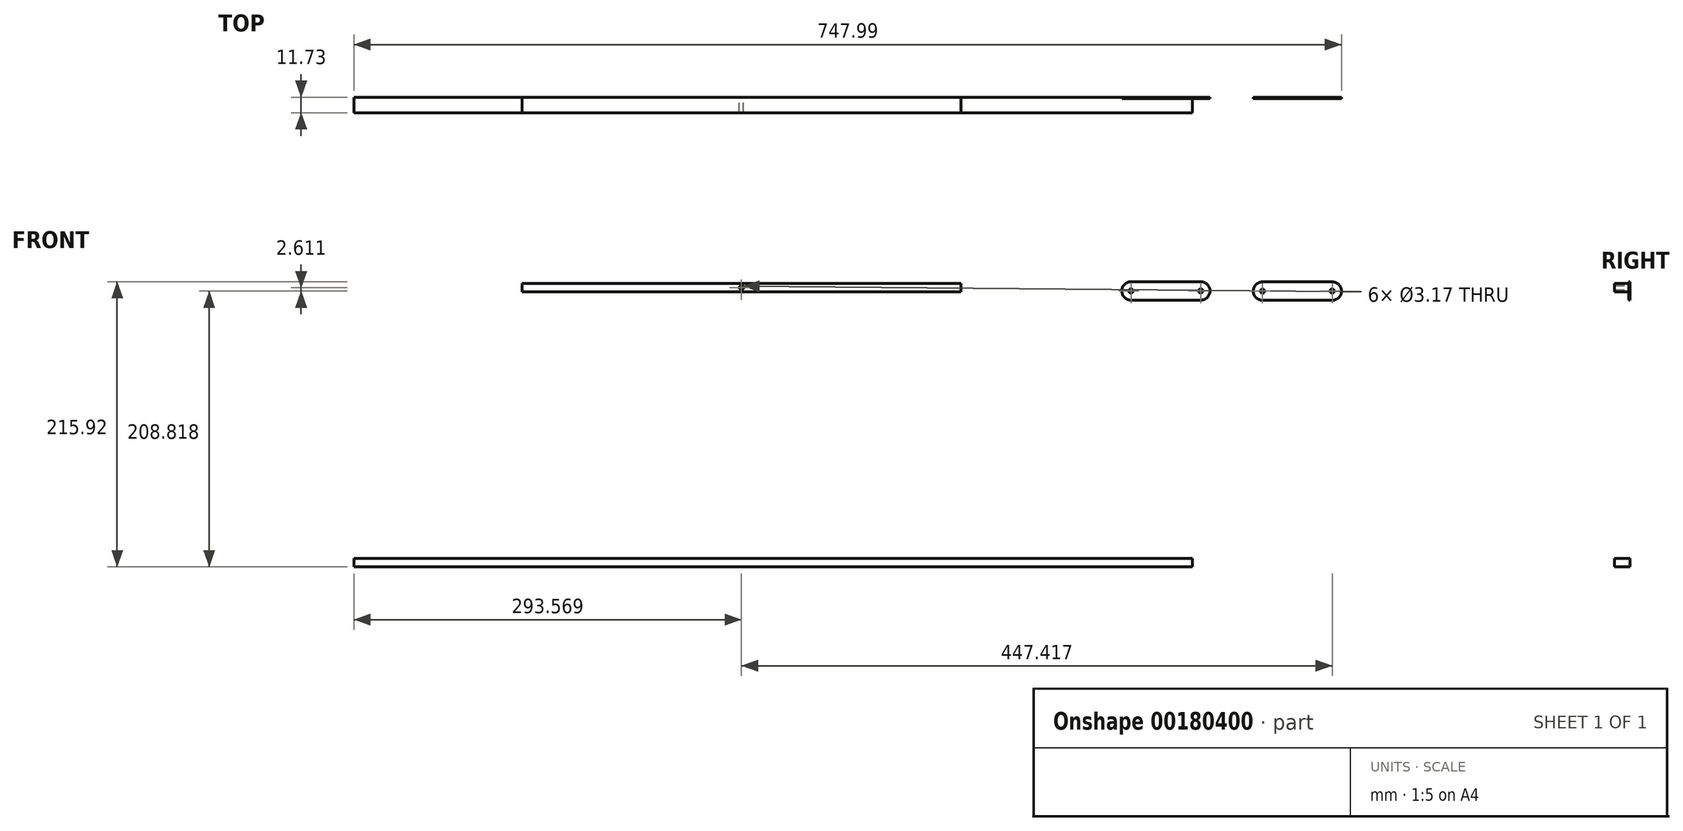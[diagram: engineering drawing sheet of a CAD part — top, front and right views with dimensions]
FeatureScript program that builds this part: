
annotation { "Feature Type Name" : "Feature", "Feature Type Description" : "" }
export const myFeature = defineFeature(function(context is Context, id is Id, definition is map)
    precondition{}
    {
        {
            var Q0;
            Q0=qCreatedBy(makeId("Front.planeOp"),FACE);
            var sketch = newSketch(context, id + "F0", { "sketchPlane" : qUnion([Q0])});
            skLineSegment(sketch, "E0.bottom", {"start": v(-373.69, -26.05) * mm, "end": v(261.31, -26.05) * mm});
            skLineSegment(sketch, "E0.top", {"start": v(-373.69, -32.4) * mm, "end": v(261.31, -32.4) * mm});
            skLineSegment(sketch, "E0.left", {"start": v(-373.69, -26.05) * mm, "end": v(-373.69, -32.4) * mm});
            skLineSegment(sketch, "E0.right", {"start": v(261.31, -26.05) * mm, "end": v(261.31, -32.4) * mm});
            skLineSegment(sketch, "E1.bottom", {"start": v(-246.19, 182.2) * mm, "end": v(85.94, 182.2) * mm});
            skLineSegment(sketch, "E1.top", {"start": v(-246.19, 175.85) * mm, "end": v(85.94, 175.85) * mm});
            skLineSegment(sketch, "E1.left", {"start": v(-246.19, 182.2) * mm, "end": v(-246.19, 175.85) * mm});
            skLineSegment(sketch, "E1.right", {"start": v(85.94, 182.2) * mm, "end": v(85.94, 175.85) * mm});
            skLineSegment(sketch, "E2", {"start": v(-80.12, 175.85) * mm, "end": v(-80.12, 182.2) * mm, "construction": true});
            skLineSegment(sketch, "E3", {"start": v(-246.19, 179.03) * mm, "end": v(85.94, 179.03) * mm, "construction": true});
            skCircle(sketch, "E4", {"center": v(-80.12, 179.03) * mm, "radius": 1.59 * mm});
            skSolve(sketch);
        }
        {
            var Q0;
            Q0=qSketchRegion(id+"F0",true);
            extrude(context, id + "F1", {"entities" : qUnion([Q0]), "depth" : 11.73 * mm});
        }
        {
            var Q0;
            Q0=qSketchRegion(id+"F0",true);
            extrude(context, id + "F2", {"entities" : qUnion([Q0]), "depth" : 11.73 * mm});
        }
        {
            var Q0;
            Q0=qCreatedBy(makeId("Front.planeOp"),FACE);
            var sketch = newSketch(context, id + "F3", { "sketchPlane" : qUnion([Q0])});
            skLineSegment(sketch, "E5", {"start": v(214.9, 183.52) * mm, "end": v(267.73, 183.52) * mm});
            skLineSegment(sketch, "E6", {"start": v(214.9, 169.5) * mm, "end": v(267.73, 169.5) * mm});
            skArc(sketch, "E7", {"start": v(214.9, 183.52) * mm, "mid": v(207.89, 176.51) * mm, "end": v(214.9, 169.5) * mm});
            skArc(sketch, "E8", {"start": v(267.73, 169.5) * mm, "mid": v(274.73, 176.51) * mm, "end": v(267.73, 183.52) * mm});
            skLineSegment(sketch, "E9", {"start": v(314.46, 183.42) * mm, "end": v(367.3, 183.42) * mm});
            skLineSegment(sketch, "E10", {"start": v(314.46, 169.41) * mm, "end": v(367.3, 169.41) * mm});
            skArc(sketch, "E11", {"start": v(314.46, 183.42) * mm, "mid": v(307.46, 176.42) * mm, "end": v(314.46, 169.41) * mm});
            skArc(sketch, "E12", {"start": v(367.3, 169.41) * mm, "mid": v(374.3, 176.42) * mm, "end": v(367.3, 183.42) * mm});
            skCircle(sketch, "E13", {"center": v(214.9, 176.51) * mm, "radius": 1.59 * mm});
            skCircle(sketch, "E14", {"center": v(267.73, 176.51) * mm, "radius": 1.59 * mm});
            skCircle(sketch, "E15", {"center": v(314.46, 176.42) * mm, "radius": 1.59 * mm});
            skCircle(sketch, "E16", {"center": v(367.3, 176.42) * mm, "radius": 1.59 * mm});
            skSolve(sketch);
        }
        {
            var Q0;
            Q0=qSketchRegion(id+"F3",true);
            extrude(context, id + "F4", {"entities" : qUnion([Q0]), "depth" : 1.02 * mm});
        }
    });
